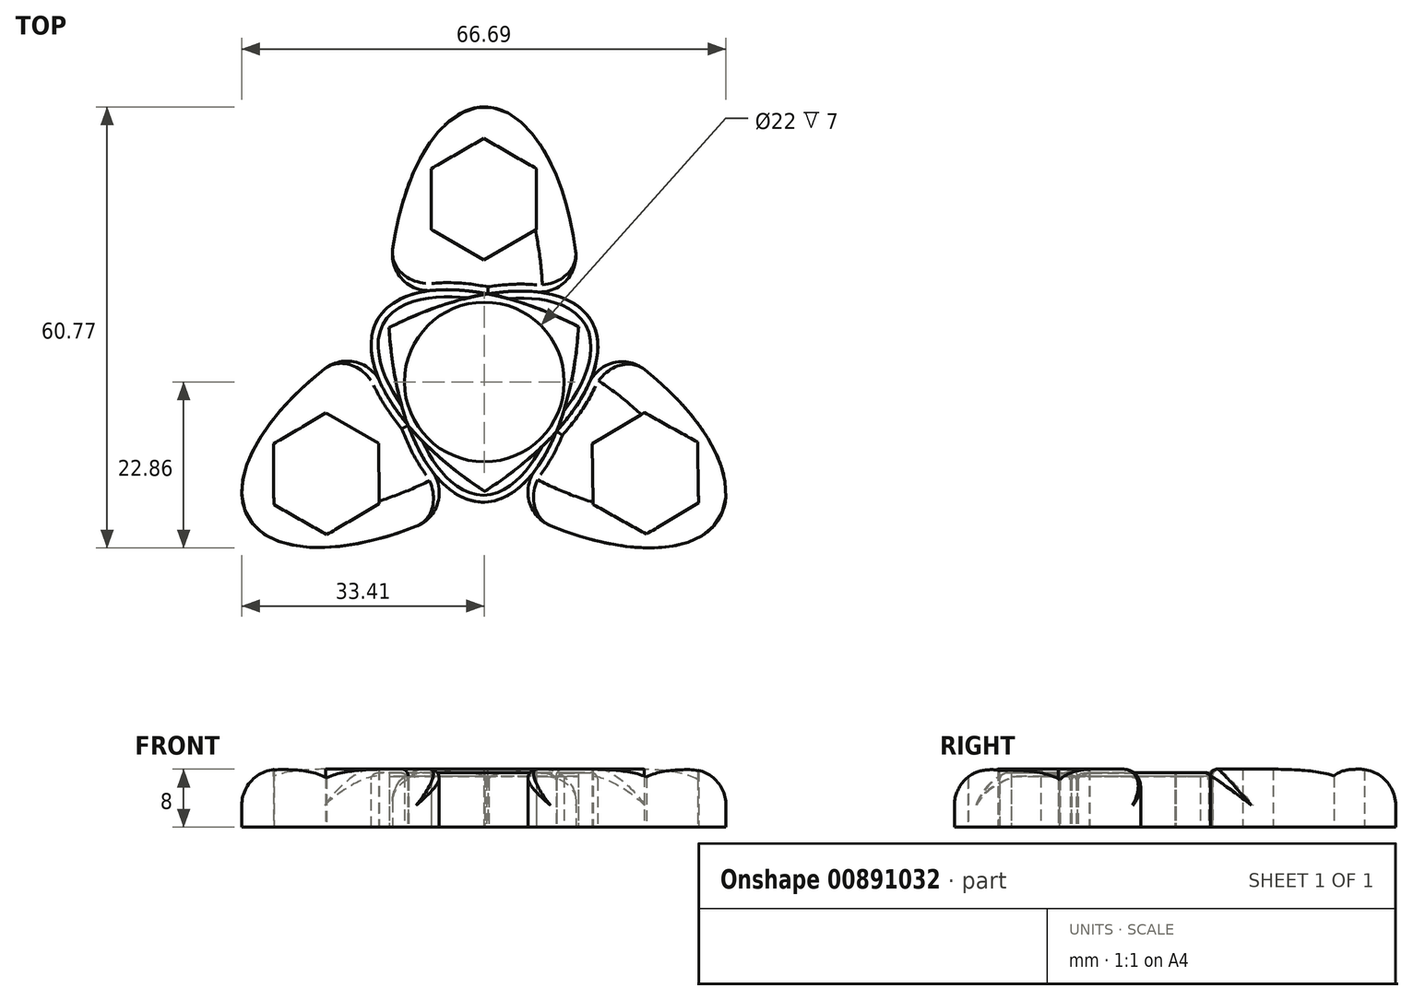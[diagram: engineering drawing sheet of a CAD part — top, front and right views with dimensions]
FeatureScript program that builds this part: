
annotation { "Feature Type Name" : "Feature", "Feature Type Description" : "" }
export const myFeature = defineFeature(function(context is Context, id is Id, definition is map)
    precondition{}
    {
        {
            var Q0;
            Q0=qCreatedBy(makeId("Top.planeOp"),FACE);
            var sketch = newSketch(context, id + "F0", { "sketchPlane" : qUnion([Q0])});
            skCircle(sketch, "E0", {"center": v(0, 0) * mm, "radius": 11 * mm});
            skSolve(sketch);
        }
        {
            var Q0;
            Q0=qCreatedBy(makeId("Top.planeOp"),FACE);
            var sketch = newSketch(context, id + "F1", { "sketchPlane" : qUnion([Q0])});
            skCircle(sketch, "E1.cCircle", {"center": v(22.18, -12.6) * mm, "radius": 7.25 * mm, "construction": true});
            skLineSegment(sketch, "E1.0", {"start": v(14.86, -8.53) * mm, "end": v(22.04, -4.22) * mm});
            skLineSegment(sketch, "E1.1", {"start": v(22.04, -4.22) * mm, "end": v(29.36, -8.29) * mm});
            skLineSegment(sketch, "E1.2", {"start": v(29.36, -8.29) * mm, "end": v(29.5, -16.66) * mm});
            skLineSegment(sketch, "E1.3", {"start": v(29.5, -16.66) * mm, "end": v(22.32, -20.96) * mm});
            skLineSegment(sketch, "E1.4", {"start": v(22.32, -20.96) * mm, "end": v(15, -16.9) * mm});
            skLineSegment(sketch, "E1.5", {"start": v(15, -16.9) * mm, "end": v(14.86, -8.53) * mm});
            skPoint(sketch, "E1.0.midPoint", {"position": v(18.45, -6.38) * mm});
            skCircle(sketch, "E2.cCircle", {"center": v(-0.07, 25.21) * mm, "radius": 7.25 * mm, "construction": true});
            skLineSegment(sketch, "E2.0", {"start": v(-7.32, 29.4) * mm, "end": v(-0.07, 33.59) * mm});
            skLineSegment(sketch, "E2.1", {"start": v(-0.07, 33.59) * mm, "end": v(7.18, 29.4) * mm});
            skLineSegment(sketch, "E2.2", {"start": v(7.18, 29.4) * mm, "end": v(7.17, 21.02) * mm});
            skLineSegment(sketch, "E2.3", {"start": v(7.17, 21.02) * mm, "end": v(-0.08, 16.84) * mm});
            skLineSegment(sketch, "E2.4", {"start": v(-0.08, 16.84) * mm, "end": v(-7.33, 21.03) * mm});
            skLineSegment(sketch, "E2.5", {"start": v(-7.33, 21.03) * mm, "end": v(-7.32, 29.4) * mm});
            skPoint(sketch, "E2.0.midPoint", {"position": v(-3.7, 31.5) * mm});
            skCircle(sketch, "E3.cCircle", {"center": v(-21.77, -12.66) * mm, "radius": 7.25 * mm, "construction": true});
            skLineSegment(sketch, "E3.0", {"start": v(-21.83, -4.29) * mm, "end": v(-14.55, -8.42) * mm});
            skLineSegment(sketch, "E3.1", {"start": v(-14.55, -8.42) * mm, "end": v(-14.5, -16.8) * mm});
            skLineSegment(sketch, "E3.2", {"start": v(-14.5, -16.8) * mm, "end": v(-21.71, -21.03) * mm});
            skLineSegment(sketch, "E3.3", {"start": v(-21.71, -21.03) * mm, "end": v(-29, -16.9) * mm});
            skLineSegment(sketch, "E3.4", {"start": v(-29, -16.9) * mm, "end": v(-29.05, -8.53) * mm});
            skLineSegment(sketch, "E3.5", {"start": v(-29.05, -8.53) * mm, "end": v(-21.83, -4.29) * mm});
            skPoint(sketch, "E3.0.midPoint", {"position": v(-18.2, -6.36) * mm});
            skEllipse(sketch, "E4", {"center": v(-8.88, -5.14) * mm, "majorRadius": 27.24 * mm, "minorRadius": 13.1 * mm, "majorAxis": v(0.87, 0.5)});
            skEllipse(sketch, "E5", {"center": v(-0.07, 10.67) * mm, "majorRadius": 27.24 * mm, "minorRadius": 13.1 * mm, "majorAxis": v(0, 1)});
            skEllipse(sketch, "E6", {"center": v(8.84, -5.07) * mm, "majorRadius": 27.24 * mm, "minorRadius": 13.1 * mm, "majorAxis": v(0.86, -0.5)});
            skSolve(sketch);
        }
        {
            var Q0;
            Q0=makeQuery(id+"F1.imprint","IMPRINT",FACE,{"disambiguationData":[TD([[makeQuery(id+"F1.imprint","IMPRINT",EDGE,{"derivedFrom":sQuery(id+"F1.wireOp",EDGE,"E2.0")}),1.0]])]});
            var Q1;
            Q1=makeQuery(id+"F1.imprint","IMPRINT",FACE,{"disambiguationData":[TD([[makeQuery(id+"F1.imprint","IMPRINT",EDGE,{"derivedFrom":sQuery(id+"F1.wireOp",EDGE,"E1.0")}),1.0]])]});
            var Q2;
            Q2=makeQuery(id+"F1.imprint","IMPRINT",FACE,{"disambiguationData":[TD([[makeQuery(id+"F1.imprint","IMPRINT",EDGE,{"derivedFrom":sQuery(id+"F1.wireOp",EDGE,"E3.0")}),1.0]])]});
            extrude(context, id + "F2", {"entities" : qUnion([Q0, Q1, Q2]), "depth" : 8 * mm, "offsetDistance" : 25 * mm});
        }
        {
            var Q0;
            {var subQ1=sQuery(id+"F1.wireOp",EDGE,"E4");var subQ3=sQuery(id+"F1.wireOp",EDGE,"E6");var subQ8=makeQuery(id+"F1.imprint","INTERSECT",VERTEX,{"disambiguationData":[OD(2.0)],"derivedFrom":[subQ1,subQ3]});Q0=makeQuery(id+"F1.imprint","IMPRINT",FACE,{"disambiguationData":[TD([[makeQuery(id+"F1.imprint","IMPRINT",EDGE,{"disambiguationData":[TD([[subQ8,-1.0]])],"derivedFrom":subQ1}),1.0]])]});}
            extrude(context, id + "F3", {"entities" : qUnion([Q0]), "depth" : 7 * mm, "offsetDistance" : 25 * mm});
        }
        {
            var Q0;
            {var subQ0=sQuery(id+"F1.wireOp",EDGE,"E6");var subQ1=sQuery(id+"F1.wireOp",EDGE,"E4");var subQ2=makeQuery(id+"F1.imprint","INTERSECT",VERTEX,{"disambiguationData":[OD(0.0)],"derivedFrom":[subQ1,subQ0]});Q0=makeQuery(id+"F1.imprint","IMPRINT",FACE,{"disambiguationData":[TD([[makeQuery(id+"F1.imprint","IMPRINT",EDGE,{"disambiguationData":[TD([[subQ2,1.0]])],"derivedFrom":subQ1}),-1.0]])]});}
            var Q1;
            {var subQ0=sQuery(id+"F1.wireOp",EDGE,"E6");var subQ1=sQuery(id+"F1.wireOp",EDGE,"E4");var subQ2=makeQuery(id+"F1.imprint","INTERSECT",VERTEX,{"disambiguationData":[OD(2.0)],"derivedFrom":[subQ1,subQ0]});Q1=makeQuery(id+"F1.imprint","IMPRINT",FACE,{"disambiguationData":[TD([[makeQuery(id+"F1.imprint","IMPRINT",EDGE,{"disambiguationData":[TD([[subQ2,-1.0]])],"derivedFrom":subQ1}),-1.0]])]});}
            var Q2;
            {var subQ0=sQuery(id+"F1.wireOp",EDGE,"E5");var subQ1=sQuery(id+"F1.wireOp",EDGE,"E4");var subQ2=makeQuery(id+"F1.imprint","INTERSECT",VERTEX,{"disambiguationData":[OD(0.0)],"derivedFrom":[subQ1,subQ0]});Q2=makeQuery(id+"F1.imprint","IMPRINT",FACE,{"disambiguationData":[TD([[makeQuery(id+"F1.imprint","IMPRINT",EDGE,{"disambiguationData":[TD([[subQ2,-1.0]])],"derivedFrom":subQ1}),1.0]])]});}
            var Q3;
            {var subQ0=sQuery(id+"F1.wireOp",EDGE,"E5");var subQ1=sQuery(id+"F1.wireOp",EDGE,"E4");var subQ2=makeQuery(id+"F1.imprint","INTERSECT",VERTEX,{"disambiguationData":[OD(0.0)],"derivedFrom":[subQ1,subQ0]});Q3=makeQuery(id+"F1.imprint","IMPRINT",FACE,{"disambiguationData":[TD([[makeQuery(id+"F1.imprint","IMPRINT",EDGE,{"disambiguationData":[TD([[subQ2,1.0]])],"derivedFrom":subQ1}),1.0]])]});}
            var Q4;
            {var subQ0=sQuery(id+"F1.wireOp",EDGE,"E6");var subQ1=sQuery(id+"F1.wireOp",EDGE,"E4");var subQ2=makeQuery(id+"F1.imprint","INTERSECT",VERTEX,{"disambiguationData":[OD(1.0)],"derivedFrom":[subQ1,subQ0]});Q4=makeQuery(id+"F1.imprint","IMPRINT",FACE,{"disambiguationData":[TD([[makeQuery(id+"F1.imprint","IMPRINT",EDGE,{"disambiguationData":[TD([[subQ2,1.0]])],"derivedFrom":subQ1}),1.0]])]});}
            var Q5;
            {var subQ0=sQuery(id+"F1.wireOp",EDGE,"E6");var subQ1=sQuery(id+"F1.wireOp",EDGE,"E4");var subQ2=makeQuery(id+"F1.imprint","INTERSECT",VERTEX,{"disambiguationData":[OD(3.0)],"derivedFrom":[subQ1,subQ0]});Q5=makeQuery(id+"F1.imprint","IMPRINT",FACE,{"disambiguationData":[TD([[makeQuery(id+"F1.imprint","IMPRINT",EDGE,{"disambiguationData":[TD([[subQ2,-1.0]])],"derivedFrom":subQ1}),-1.0]])]});}
            var Q6;
            {var subQ0=sQuery(id+"F1.wireOp",EDGE,"E5");var subQ1=sQuery(id+"F1.wireOp",EDGE,"E4");var subQ2=makeQuery(id+"F1.imprint","INTERSECT",VERTEX,{"disambiguationData":[OD(1.0)],"derivedFrom":[subQ1,subQ0]});Q6=makeQuery(id+"F1.imprint","IMPRINT",FACE,{"disambiguationData":[TD([[makeQuery(id+"F1.imprint","IMPRINT",EDGE,{"disambiguationData":[TD([[subQ2,-1.0]])],"derivedFrom":subQ1}),-1.0]])]});}
            var Q7;
            {var subQ0=sQuery(id+"F1.wireOp",EDGE,"E5");var subQ1=sQuery(id+"F1.wireOp",EDGE,"E4");var subQ2=makeQuery(id+"F1.imprint","INTERSECT",VERTEX,{"disambiguationData":[OD(1.0)],"derivedFrom":[subQ1,subQ0]});Q7=makeQuery(id+"F1.imprint","IMPRINT",FACE,{"disambiguationData":[TD([[makeQuery(id+"F1.imprint","IMPRINT",EDGE,{"disambiguationData":[TD([[subQ2,-1.0]])],"derivedFrom":subQ1}),1.0]])]});}
            var Q8;
            {var subQ0=sQuery(id+"F1.wireOp",EDGE,"E6");var subQ1=sQuery(id+"F1.wireOp",EDGE,"E4");var subQ2=makeQuery(id+"F1.imprint","INTERSECT",VERTEX,{"disambiguationData":[OD(0.0)],"derivedFrom":[subQ1,subQ0]});Q8=makeQuery(id+"F1.imprint","IMPRINT",FACE,{"disambiguationData":[TD([[makeQuery(id+"F1.imprint","IMPRINT",EDGE,{"disambiguationData":[TD([[subQ2,1.0]])],"derivedFrom":subQ1}),1.0]])]});}
            extrude(context, id + "F4", {"entities" : qUnion([Q0, Q1, Q2, Q3, Q4, Q5, Q6, Q7, Q8]), "depth" : 7.5 * mm, "offsetDistance" : 25 * mm});
        }
        {
            var Q0;
            Q0 = qSketchRegion(id + "F0", true);
            extrude(context, id + "F5", {"entities" : qUnion([Q0]), "operationType" : NewBodyOperationType.REMOVE, "depth" : 15.2 * mm, "offsetDistance" : 25 * mm});
        }
        {
            var Q0;
            {var subQ0=sQuery(id+"F1.wireOp",EDGE,"E6");Q0=makeQuery(id+"F2.opExtrude","CAP_EDGE",EDGE,{"disambiguationData":[OSD([subQ0]),TDD([makeQuery(id+"F1.imprint","IMPRINT",EDGE,{"disambiguationData":[TD([[makeQuery(id+"F1.imprint","INTERSECT",VERTEX,{"disambiguationData":[OD(0.0)],"derivedFrom":[sQuery(id+"F1.wireOp",EDGE,"E5"),subQ0]}),1.0]])],"derivedFrom":subQ0})])],"isStart":false});}
            var Q1;
            {var subQ0=sQuery(id+"F1.wireOp",EDGE,"E4");Q1=makeQuery(id+"F2.opExtrude","CAP_EDGE",EDGE,{"disambiguationData":[OSD([subQ0]),TDD([makeQuery(id+"F1.imprint","IMPRINT",EDGE,{"disambiguationData":[TD([[makeQuery(id+"F1.imprint","INTERSECT",VERTEX,{"disambiguationData":[OD(0.0)],"derivedFrom":[subQ0,sQuery(id+"F1.wireOp",EDGE,"E5")]}),-1.0]])],"derivedFrom":subQ0})])],"isStart":false});}
            var Q2;
            {var subQ0=sQuery(id+"F1.wireOp",EDGE,"E6");Q2=makeQuery(id+"F2.opExtrude","CAP_EDGE",EDGE,{"disambiguationData":[OSD([subQ0]),TDD([makeQuery(id+"F1.imprint","IMPRINT",EDGE,{"disambiguationData":[TD([[makeQuery(id+"F1.imprint","INTERSECT",VERTEX,{"disambiguationData":[OD(0.0)],"derivedFrom":[sQuery(id+"F1.wireOp",EDGE,"E4"),subQ0]}),-1.0]])],"derivedFrom":subQ0})])],"isStart":false});}
            var Q3;
            {var subQ0=sQuery(id+"F1.wireOp",EDGE,"E5");Q3=makeQuery(id+"F2.opExtrude","CAP_EDGE",EDGE,{"disambiguationData":[OSD([subQ0]),TDD([makeQuery(id+"F1.imprint","IMPRINT",EDGE,{"disambiguationData":[TD([[makeQuery(id+"F1.imprint","INTERSECT",VERTEX,{"disambiguationData":[OD(1.0)],"derivedFrom":[subQ0,sQuery(id+"F1.wireOp",EDGE,"E6")]}),-1.0]])],"derivedFrom":subQ0})])],"isStart":false});}
            var Q4;
            {var subQ0=sQuery(id+"F1.wireOp",EDGE,"E4");Q4=makeQuery(id+"F2.opExtrude","CAP_EDGE",EDGE,{"disambiguationData":[OSD([subQ0]),TDD([makeQuery(id+"F1.imprint","IMPRINT",EDGE,{"disambiguationData":[TD([[makeQuery(id+"F1.imprint","INTERSECT",VERTEX,{"disambiguationData":[OD(1.0)],"derivedFrom":[subQ0,sQuery(id+"F1.wireOp",EDGE,"E6")]}),1.0]])],"derivedFrom":subQ0})])],"isStart":false});}
            var Q5;
            {var subQ0=sQuery(id+"F1.wireOp",EDGE,"E5");Q5=makeQuery(id+"F2.opExtrude","CAP_EDGE",EDGE,{"disambiguationData":[OSD([subQ0]),TDD([makeQuery(id+"F1.imprint","IMPRINT",EDGE,{"disambiguationData":[TD([[makeQuery(id+"F1.imprint","INTERSECT",VERTEX,{"disambiguationData":[OD(1.0)],"derivedFrom":[sQuery(id+"F1.wireOp",EDGE,"E4"),subQ0]}),1.0]])],"derivedFrom":subQ0})])],"isStart":false});}
            fillet(context, id + "F6", {"entities" : qUnion([Q0, Q1, Q2, Q3, Q4, Q5]), "radius" : 0.97 * mm, "tangentPropagation" : true, "allowEdgeOverflow" : false});
        }
        {
            var Q0;
            {var subQ0=sQuery(id+"F1.wireOp",EDGE,"E6");Q0=makeQuery(id+"F2.opExtrude","CAP_EDGE",EDGE,{"disambiguationData":[OSD([subQ0]),TDD([makeQuery(id+"F1.imprint","IMPRINT",EDGE,{"disambiguationData":[TD([[makeQuery(id+"F1.imprint","INTERSECT",VERTEX,{"disambiguationData":[OD(1.0)],"derivedFrom":[sQuery(id+"F1.wireOp",EDGE,"E4"),subQ0]}),1.0]])],"derivedFrom":subQ0})])],"isStart":false});}
            var Q1;
            {var subQ0=sQuery(id+"F1.wireOp",EDGE,"E5");Q1=makeQuery(id+"F2.opExtrude","CAP_EDGE",EDGE,{"disambiguationData":[OSD([subQ0]),TDD([makeQuery(id+"F1.imprint","IMPRINT",EDGE,{"disambiguationData":[TD([[makeQuery(id+"F1.imprint","INTERSECT",VERTEX,{"disambiguationData":[OD(0.0)],"derivedFrom":[sQuery(id+"F1.wireOp",EDGE,"E4"),subQ0]}),-1.0]])],"derivedFrom":subQ0})])],"isStart":false});}
            var Q2;
            {var subQ0=sQuery(id+"F1.wireOp",EDGE,"E4");Q2=makeQuery(id+"F2.opExtrude","CAP_EDGE",EDGE,{"disambiguationData":[OSD([subQ0]),TDD([makeQuery(id+"F1.imprint","IMPRINT",EDGE,{"disambiguationData":[TD([[makeQuery(id+"F1.imprint","INTERSECT",VERTEX,{"disambiguationData":[OD(0.0)],"derivedFrom":[subQ0,sQuery(id+"F1.wireOp",EDGE,"E6")]}),-1.0]])],"derivedFrom":subQ0})])],"isStart":false});}
            fillet(context, id + "F7", {"entities" : qUnion([Q0, Q1, Q2]), "radius" : 5 * mm, "tangentPropagation" : true, "allowEdgeOverflow" : false});
        }
        {
            var Q0;
            {var subQ0=sQuery(id+"F1.wireOp",EDGE,"E6");var subQ1=sQuery(id+"F1.wireOp",EDGE,"E5");var subQ2=makeQuery(id+"F1.imprint","INTERSECT",VERTEX,{"disambiguationData":[OD(1.0)],"derivedFrom":[subQ1,subQ0]});var subQ3=sQuery(id+"F1.wireOp",EDGE,"E4");var subQ4=makeQuery(id+"F1.imprint","INTERSECT",VERTEX,{"disambiguationData":[OD(1.0)],"derivedFrom":[subQ3,subQ1]});Q0=makeQuery(id+"F4.opExtrude","CAP_EDGE",EDGE,{"disambiguationData":[OSD([subQ1]),TDD([makeQuery(id+"F1.imprint","IMPRINT",EDGE,{"disambiguationData":[TD([[subQ4,1.0]])],"derivedFrom":subQ1}),makeQuery(id+"F1.imprint","IMPRINT",EDGE,{"disambiguationData":[TD([[subQ4,-1.0]])],"derivedFrom":subQ1}),makeQuery(id+"F1.imprint","IMPRINT",EDGE,{"disambiguationData":[TD([[subQ2,-1.0]])],"derivedFrom":subQ1})])],"isStart":false});}
            var Q1;
            {var subQ0=sQuery(id+"F1.wireOp",EDGE,"E5");var subQ1=sQuery(id+"F1.wireOp",EDGE,"E4");var subQ2=makeQuery(id+"F1.imprint","INTERSECT",VERTEX,{"disambiguationData":[OD(0.0)],"derivedFrom":[subQ1,subQ0]});var subQ3=sQuery(id+"F1.wireOp",EDGE,"E6");var subQ4=makeQuery(id+"F1.imprint","INTERSECT",VERTEX,{"disambiguationData":[OD(1.0)],"derivedFrom":[subQ1,subQ3]});Q1=makeQuery(id+"F4.opExtrude","CAP_EDGE",EDGE,{"disambiguationData":[OSD([subQ1]),TDD([makeQuery(id+"F1.imprint","IMPRINT",EDGE,{"disambiguationData":[TD([[subQ2,-1.0]])],"derivedFrom":subQ1}),makeQuery(id+"F1.imprint","IMPRINT",EDGE,{"disambiguationData":[TD([[subQ4,1.0]])],"derivedFrom":subQ1}),makeQuery(id+"F1.imprint","IMPRINT",EDGE,{"disambiguationData":[TD([[subQ2,1.0]])],"derivedFrom":subQ1})])],"isStart":false});}
            var Q2;
            {var subQ0=sQuery(id+"F1.wireOp",EDGE,"E6");var subQ1=sQuery(id+"F1.wireOp",EDGE,"E4");var subQ2=makeQuery(id+"F1.imprint","INTERSECT",VERTEX,{"disambiguationData":[OD(0.0)],"derivedFrom":[subQ1,subQ0]});var subQ3=sQuery(id+"F1.wireOp",EDGE,"E5");var subQ4=makeQuery(id+"F1.imprint","INTERSECT",VERTEX,{"disambiguationData":[OD(0.0)],"derivedFrom":[subQ3,subQ0]});Q2=makeQuery(id+"F4.opExtrude","CAP_EDGE",EDGE,{"disambiguationData":[OSD([subQ0]),TDD([makeQuery(id+"F1.imprint","IMPRINT",EDGE,{"disambiguationData":[TD([[subQ4,1.0]])],"derivedFrom":subQ0}),makeQuery(id+"F1.imprint","IMPRINT",EDGE,{"disambiguationData":[TD([[subQ2,1.0]])],"derivedFrom":subQ0}),makeQuery(id+"F1.imprint","IMPRINT",EDGE,{"disambiguationData":[TD([[subQ2,-1.0]])],"derivedFrom":subQ0})])],"isStart":false});}
            fillet(context, id + "F8", {"entities" : qUnion([Q0, Q1, Q2]), "radius" : 0.97 * mm, "tangentPropagation" : true, "allowEdgeOverflow" : false});
        }
        {
            var Q0;
            {var subQ0=sQuery(id+"F1.wireOp",EDGE,"E5");Q0=makeQuery(id+"F4.opExtrude","CAP_EDGE",EDGE,{"disambiguationData":[OSD([subQ0]),TDD([makeQuery(id+"F1.imprint","IMPRINT",EDGE,{"disambiguationData":[TD([[makeQuery(id+"F1.imprint","INTERSECT",VERTEX,{"disambiguationData":[OD(3.0)],"derivedFrom":[sQuery(id+"F1.wireOp",EDGE,"E4"),subQ0]}),-1.0]])],"derivedFrom":subQ0})])],"isStart":false});}
            var Q1;
            {var subQ0=sQuery(id+"F1.wireOp",EDGE,"E4");Q1=makeQuery(id+"F4.opExtrude","CAP_EDGE",EDGE,{"disambiguationData":[OSD([subQ0]),TDD([makeQuery(id+"F1.imprint","IMPRINT",EDGE,{"disambiguationData":[TD([[makeQuery(id+"F1.imprint","INTERSECT",VERTEX,{"disambiguationData":[OD(3.0)],"derivedFrom":[subQ0,sQuery(id+"F1.wireOp",EDGE,"E6")]}),-1.0]])],"derivedFrom":subQ0})])],"isStart":false});}
            var Q2;
            {var subQ0=sQuery(id+"F1.wireOp",EDGE,"E6");Q2=makeQuery(id+"F4.opExtrude","CAP_EDGE",EDGE,{"disambiguationData":[OSD([subQ0]),TDD([makeQuery(id+"F1.imprint","IMPRINT",EDGE,{"disambiguationData":[TD([[makeQuery(id+"F1.imprint","INTERSECT",VERTEX,{"disambiguationData":[OD(2.0)],"derivedFrom":[sQuery(id+"F1.wireOp",EDGE,"E4"),subQ0]}),1.0]])],"derivedFrom":subQ0})])],"isStart":false});}
            var Q3;
            {var subQ0=sQuery(id+"F1.wireOp",EDGE,"E6");Q3=makeQuery(id+"F4.opExtrude","CAP_EDGE",EDGE,{"disambiguationData":[OSD([subQ0]),TDD([makeQuery(id+"F1.imprint","IMPRINT",EDGE,{"disambiguationData":[TD([[makeQuery(id+"F1.imprint","INTERSECT",VERTEX,{"disambiguationData":[OD(3.0)],"derivedFrom":[sQuery(id+"F1.wireOp",EDGE,"E4"),subQ0]}),1.0]])],"derivedFrom":subQ0})])],"isStart":false});}
            var Q4;
            {var subQ0=sQuery(id+"F1.wireOp",EDGE,"E5");Q4=makeQuery(id+"F4.opExtrude","CAP_EDGE",EDGE,{"disambiguationData":[OSD([subQ0]),TDD([makeQuery(id+"F1.imprint","IMPRINT",EDGE,{"disambiguationData":[TD([[makeQuery(id+"F1.imprint","INTERSECT",VERTEX,{"disambiguationData":[OD(2.0)],"derivedFrom":[sQuery(id+"F1.wireOp",EDGE,"E4"),subQ0]}),-1.0]])],"derivedFrom":subQ0})])],"isStart":false});}
            var Q5;
            {var subQ0=sQuery(id+"F1.wireOp",EDGE,"E4");Q5=makeQuery(id+"F4.opExtrude","CAP_EDGE",EDGE,{"disambiguationData":[OSD([subQ0]),TDD([makeQuery(id+"F1.imprint","IMPRINT",EDGE,{"disambiguationData":[TD([[makeQuery(id+"F1.imprint","INTERSECT",VERTEX,{"disambiguationData":[OD(2.0)],"derivedFrom":[subQ0,sQuery(id+"F1.wireOp",EDGE,"E6")]}),-1.0]])],"derivedFrom":subQ0})])],"isStart":false});}
            var Q6;
            {var subQ0=sQuery(id+"F1.wireOp",EDGE,"E6");var subQ1=sQuery(id+"F1.wireOp",EDGE,"E4");var subQ2=makeQuery(id+"F1.imprint","INTERSECT",VERTEX,{"disambiguationData":[OD(2.0)],"derivedFrom":[subQ1,subQ0]});var subQ3=sQuery(id+"F1.wireOp",EDGE,"E5");var subQ4=makeQuery(id+"F1.imprint","INTERSECT",VERTEX,{"disambiguationData":[OD(0.0)],"derivedFrom":[subQ1,subQ0]});var subQ5=makeQuery(id+"F1.imprint","INTERSECT",VERTEX,{"disambiguationData":[OD(0.0)],"derivedFrom":[subQ3,subQ0]});Q6=makeQuery(id+"F8.opFillet","BLEND_EDGE",EDGE,{"blendedFrom":[makeQuery(id+"F4.opExtrude","CAP_EDGE",EDGE,{"disambiguationData":[OSD([subQ0]),TDD([makeQuery(id+"F1.imprint","IMPRINT",EDGE,{"disambiguationData":[TD([[subQ5,1.0]])],"derivedFrom":subQ0}),makeQuery(id+"F1.imprint","IMPRINT",EDGE,{"disambiguationData":[TD([[subQ4,1.0]])],"derivedFrom":subQ0}),makeQuery(id+"F1.imprint","IMPRINT",EDGE,{"disambiguationData":[TD([[subQ4,-1.0]])],"derivedFrom":subQ0})])],"isStart":false}),makeQuery(id+"F4.opExtrude","SWEPT_FACE",FACE,{"disambiguationData":[OSD([subQ1]),TDD([makeQuery(id+"F1.imprint","IMPRINT",EDGE,{"disambiguationData":[TD([[subQ2,-1.0]])],"derivedFrom":subQ1})])]})],"blendedInto":[makeQuery(id+"F4.opExtrude","SWEPT_FACE",FACE,{"disambiguationData":[OSD([subQ1]),TDD([makeQuery(id+"F1.imprint","IMPRINT",EDGE,{"disambiguationData":[TD([[subQ2,-1.0]])],"derivedFrom":subQ1})])]})]});}
            var Q7;
            {var subQ0=sQuery(id+"F1.wireOp",EDGE,"E6");var subQ1=sQuery(id+"F1.wireOp",EDGE,"E4");var subQ2=makeQuery(id+"F1.imprint","INTERSECT",VERTEX,{"disambiguationData":[OD(2.0)],"derivedFrom":[subQ1,subQ0]});var subQ3=sQuery(id+"F1.wireOp",EDGE,"E5");var subQ4=makeQuery(id+"F1.imprint","INTERSECT",VERTEX,{"disambiguationData":[OD(0.0)],"derivedFrom":[subQ1,subQ3]});var subQ5=makeQuery(id+"F1.imprint","INTERSECT",VERTEX,{"disambiguationData":[OD(1.0)],"derivedFrom":[subQ1,subQ0]});Q7=makeQuery(id+"F8.opFillet","BLEND_EDGE",EDGE,{"blendedFrom":[makeQuery(id+"F4.opExtrude","CAP_EDGE",EDGE,{"disambiguationData":[OSD([subQ1]),TDD([makeQuery(id+"F1.imprint","IMPRINT",EDGE,{"disambiguationData":[TD([[subQ4,-1.0]])],"derivedFrom":subQ1}),makeQuery(id+"F1.imprint","IMPRINT",EDGE,{"disambiguationData":[TD([[subQ5,1.0]])],"derivedFrom":subQ1}),makeQuery(id+"F1.imprint","IMPRINT",EDGE,{"disambiguationData":[TD([[subQ4,1.0]])],"derivedFrom":subQ1})])],"isStart":false}),makeQuery(id+"F4.opExtrude","SWEPT_FACE",FACE,{"disambiguationData":[OSD([subQ0]),TDD([makeQuery(id+"F1.imprint","IMPRINT",EDGE,{"disambiguationData":[TD([[subQ2,1.0]])],"derivedFrom":subQ0})])]})],"blendedInto":[makeQuery(id+"F4.opExtrude","SWEPT_FACE",FACE,{"disambiguationData":[OSD([subQ0]),TDD([makeQuery(id+"F1.imprint","IMPRINT",EDGE,{"disambiguationData":[TD([[subQ2,1.0]])],"derivedFrom":subQ0})])]})]});}
            var Q8;
            {var subQ0=sQuery(id+"F1.wireOp",EDGE,"E5");var subQ1=sQuery(id+"F1.wireOp",EDGE,"E4");var subQ2=makeQuery(id+"F1.imprint","INTERSECT",VERTEX,{"disambiguationData":[OD(3.0)],"derivedFrom":[subQ1,subQ0]});var subQ3=sQuery(id+"F1.wireOp",EDGE,"E6");var subQ4=makeQuery(id+"F1.imprint","INTERSECT",VERTEX,{"disambiguationData":[OD(0.0)],"derivedFrom":[subQ1,subQ0]});var subQ5=makeQuery(id+"F1.imprint","INTERSECT",VERTEX,{"disambiguationData":[OD(1.0)],"derivedFrom":[subQ1,subQ3]});Q8=makeQuery(id+"F8.opFillet","BLEND_EDGE",EDGE,{"blendedFrom":[makeQuery(id+"F4.opExtrude","CAP_EDGE",EDGE,{"disambiguationData":[OSD([subQ1]),TDD([makeQuery(id+"F1.imprint","IMPRINT",EDGE,{"disambiguationData":[TD([[subQ4,-1.0]])],"derivedFrom":subQ1}),makeQuery(id+"F1.imprint","IMPRINT",EDGE,{"disambiguationData":[TD([[subQ5,1.0]])],"derivedFrom":subQ1}),makeQuery(id+"F1.imprint","IMPRINT",EDGE,{"disambiguationData":[TD([[subQ4,1.0]])],"derivedFrom":subQ1})])],"isStart":false}),makeQuery(id+"F4.opExtrude","SWEPT_FACE",FACE,{"disambiguationData":[OSD([subQ0]),TDD([makeQuery(id+"F1.imprint","IMPRINT",EDGE,{"disambiguationData":[TD([[subQ2,-1.0]])],"derivedFrom":subQ0})])]})],"blendedInto":[makeQuery(id+"F4.opExtrude","SWEPT_FACE",FACE,{"disambiguationData":[OSD([subQ0]),TDD([makeQuery(id+"F1.imprint","IMPRINT",EDGE,{"disambiguationData":[TD([[subQ2,-1.0]])],"derivedFrom":subQ0})])]})]});}
            var Q9;
            {var subQ0=sQuery(id+"F1.wireOp",EDGE,"E6");var subQ1=sQuery(id+"F1.wireOp",EDGE,"E4");var subQ2=sQuery(id+"F1.wireOp",EDGE,"E5");var subQ4=makeQuery(id+"F1.imprint","INTERSECT",VERTEX,{"disambiguationData":[OD(1.0)],"derivedFrom":[subQ2,subQ0]});var subQ5=makeQuery(id+"F1.imprint","INTERSECT",VERTEX,{"disambiguationData":[OD(1.0)],"derivedFrom":[subQ1,subQ2]});Q9=makeQuery(id+"F8.opFillet","BLEND_EDGE",EDGE,{"blendedFrom":[makeQuery(id+"F4.opExtrude","CAP_EDGE",EDGE,{"disambiguationData":[OSD([subQ2]),TDD([makeQuery(id+"F1.imprint","IMPRINT",EDGE,{"disambiguationData":[TD([[subQ5,1.0]])],"derivedFrom":subQ2}),makeQuery(id+"F1.imprint","IMPRINT",EDGE,{"disambiguationData":[TD([[subQ5,-1.0]])],"derivedFrom":subQ2}),makeQuery(id+"F1.imprint","IMPRINT",EDGE,{"disambiguationData":[TD([[subQ4,-1.0]])],"derivedFrom":subQ2})])],"isStart":false}),makeQuery(id+"F4.opExtrude","SWEPT_FACE",FACE,{"disambiguationData":[OSD([subQ1]),TDD([makeQuery(id+"F1.imprint","IMPRINT",EDGE,{"disambiguationData":[TD([[makeQuery(id+"F1.imprint","INTERSECT",VERTEX,{"disambiguationData":[OD(3.0)],"derivedFrom":[subQ1,subQ0]}),-1.0]])],"derivedFrom":subQ1})])]})],"blendedInto":[makeQuery(id+"F4.opExtrude","SWEPT_FACE",FACE,{"disambiguationData":[OSD([subQ1]),TDD([makeQuery(id+"F1.imprint","IMPRINT",EDGE,{"disambiguationData":[TD([[makeQuery(id+"F1.imprint","INTERSECT",VERTEX,{"disambiguationData":[OD(3.0)],"derivedFrom":[subQ1,subQ0]}),-1.0]])],"derivedFrom":subQ1})])]})]});}
            var Q10;
            {var subQ0=sQuery(id+"F1.wireOp",EDGE,"E6");var subQ1=sQuery(id+"F1.wireOp",EDGE,"E4");var subQ2=sQuery(id+"F1.wireOp",EDGE,"E5");var subQ4=makeQuery(id+"F1.imprint","INTERSECT",VERTEX,{"disambiguationData":[OD(1.0)],"derivedFrom":[subQ2,subQ0]});var subQ5=makeQuery(id+"F1.imprint","INTERSECT",VERTEX,{"disambiguationData":[OD(1.0)],"derivedFrom":[subQ1,subQ2]});Q10=makeQuery(id+"F8.opFillet","BLEND_EDGE",EDGE,{"blendedFrom":[makeQuery(id+"F4.opExtrude","CAP_EDGE",EDGE,{"disambiguationData":[OSD([subQ2]),TDD([makeQuery(id+"F1.imprint","IMPRINT",EDGE,{"disambiguationData":[TD([[subQ5,1.0]])],"derivedFrom":subQ2}),makeQuery(id+"F1.imprint","IMPRINT",EDGE,{"disambiguationData":[TD([[subQ5,-1.0]])],"derivedFrom":subQ2}),makeQuery(id+"F1.imprint","IMPRINT",EDGE,{"disambiguationData":[TD([[subQ4,-1.0]])],"derivedFrom":subQ2})])],"isStart":false}),makeQuery(id+"F4.opExtrude","SWEPT_FACE",FACE,{"disambiguationData":[OSD([subQ0]),TDD([makeQuery(id+"F1.imprint","IMPRINT",EDGE,{"disambiguationData":[TD([[makeQuery(id+"F1.imprint","INTERSECT",VERTEX,{"disambiguationData":[OD(3.0)],"derivedFrom":[subQ1,subQ0]}),1.0]])],"derivedFrom":subQ0})])]})],"blendedInto":[makeQuery(id+"F4.opExtrude","SWEPT_FACE",FACE,{"disambiguationData":[OSD([subQ0]),TDD([makeQuery(id+"F1.imprint","IMPRINT",EDGE,{"disambiguationData":[TD([[makeQuery(id+"F1.imprint","INTERSECT",VERTEX,{"disambiguationData":[OD(3.0)],"derivedFrom":[subQ1,subQ0]}),1.0]])],"derivedFrom":subQ0})])]})]});}
            var Q11;
            {var subQ0=sQuery(id+"F1.wireOp",EDGE,"E5");var subQ1=sQuery(id+"F1.wireOp",EDGE,"E4");var subQ2=sQuery(id+"F1.wireOp",EDGE,"E6");var subQ4=makeQuery(id+"F1.imprint","INTERSECT",VERTEX,{"disambiguationData":[OD(0.0)],"derivedFrom":[subQ1,subQ2]});var subQ5=makeQuery(id+"F1.imprint","INTERSECT",VERTEX,{"disambiguationData":[OD(0.0)],"derivedFrom":[subQ0,subQ2]});Q11=makeQuery(id+"F8.opFillet","BLEND_EDGE",EDGE,{"blendedFrom":[makeQuery(id+"F4.opExtrude","CAP_EDGE",EDGE,{"disambiguationData":[OSD([subQ2]),TDD([makeQuery(id+"F1.imprint","IMPRINT",EDGE,{"disambiguationData":[TD([[subQ5,1.0]])],"derivedFrom":subQ2}),makeQuery(id+"F1.imprint","IMPRINT",EDGE,{"disambiguationData":[TD([[subQ4,1.0]])],"derivedFrom":subQ2}),makeQuery(id+"F1.imprint","IMPRINT",EDGE,{"disambiguationData":[TD([[subQ4,-1.0]])],"derivedFrom":subQ2})])],"isStart":false}),makeQuery(id+"F4.opExtrude","SWEPT_FACE",FACE,{"disambiguationData":[OSD([subQ0]),TDD([makeQuery(id+"F1.imprint","IMPRINT",EDGE,{"disambiguationData":[TD([[makeQuery(id+"F1.imprint","INTERSECT",VERTEX,{"disambiguationData":[OD(2.0)],"derivedFrom":[subQ1,subQ0]}),-1.0]])],"derivedFrom":subQ0})])]})],"blendedInto":[makeQuery(id+"F4.opExtrude","SWEPT_FACE",FACE,{"disambiguationData":[OSD([subQ0]),TDD([makeQuery(id+"F1.imprint","IMPRINT",EDGE,{"disambiguationData":[TD([[makeQuery(id+"F1.imprint","INTERSECT",VERTEX,{"disambiguationData":[OD(2.0)],"derivedFrom":[subQ1,subQ0]}),-1.0]])],"derivedFrom":subQ0})])]})]});}
            fillet(context, id + "F9", {"entities" : qUnion([Q0, Q1, Q2, Q3, Q4, Q5, Q6, Q7, Q8, Q9, Q10, Q11]), "radius" : 0.03 * mm, "tangentPropagation" : true, "allowEdgeOverflow" : false});
        }
    });
